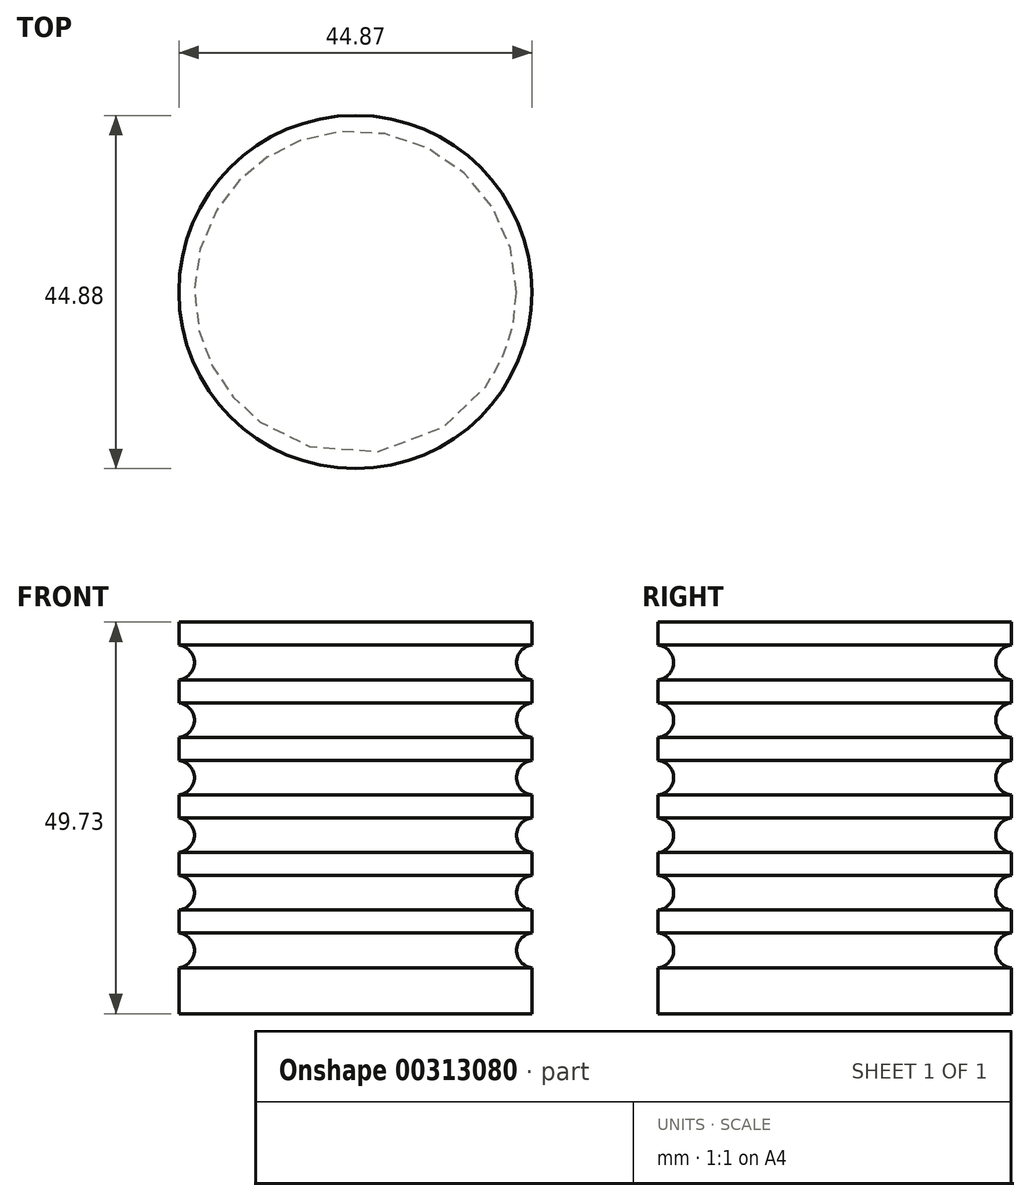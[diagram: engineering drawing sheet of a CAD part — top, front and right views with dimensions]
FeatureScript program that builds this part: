
annotation { "Feature Type Name" : "Feature", "Feature Type Description" : "" }
export const myFeature = defineFeature(function(context is Context, id is Id, definition is map)
    precondition{}
    {
        {
            var Q0;
            Q0=qCreatedBy(makeId("Front.planeOp"),FACE);
            var sketch = newSketch(context, id + "F0", { "sketchPlane" : qUnion([Q0])});
            skLineSegment(sketch, "E0.left", {"start": v(-41.76, 39.6) * mm, "end": v(-41.76, -10.14) * mm});
            skPoint(sketch, "E1.left.start.orphan", {"position": v(-35.66, 9.75) * mm});
            skPoint(sketch, "E0.bottom.end.orphan", {"position": v(-35.66, 39.17) * mm});
            skPoint(sketch, "E0.top.end.orphan", {"position": v(-35.66, -19.66) * mm});
            skLineSegment(sketch, "E2.bottom", {"start": v(-41.76, 39.6) * mm, "end": v(-19.32, 39.6) * mm});
            skLineSegment(sketch, "E2.top", {"start": v(-41.76, -10.14) * mm, "end": v(-19.32, -10.14) * mm});
            skLineSegment(sketch, "E2.right", {"start": v(-19.32, 39.6) * mm, "end": v(-19.32, 36.67) * mm});
            skArc(sketch, "E3", {"start": v(-19.32, 36.67) * mm, "mid": v(-21.3, 34.47) * mm, "end": v(-19.32, 32.28) * mm});
            skArc(sketch, "E4", {"start": v(-19.32, 29.36) * mm, "mid": v(-21.3, 27.16) * mm, "end": v(-19.32, 24.96) * mm});
            skArc(sketch, "E5", {"start": v(-19.32, 22.04) * mm, "mid": v(-21.3, 19.84) * mm, "end": v(-19.32, 17.65) * mm});
            skArc(sketch, "E6", {"start": v(-19.32, 14.73) * mm, "mid": v(-21.3, 12.53) * mm, "end": v(-19.32, 10.33) * mm});
            skArc(sketch, "E7", {"start": v(-19.32, 7.41) * mm, "mid": v(-21.3, 5.21) * mm, "end": v(-19.32, 3.02) * mm});
            skArc(sketch, "E8", {"start": v(-19.32, 0.1) * mm, "mid": v(-21.3, -2.1) * mm, "end": v(-19.32, -4.3) * mm});
            skLineSegment(sketch, "E9.trimOffspring", {"start": v(-19.32, 32.28) * mm, "end": v(-19.32, 29.36) * mm});
            skLineSegment(sketch, "E10.trimOffspring", {"start": v(-19.32, 24.96) * mm, "end": v(-19.32, 22.04) * mm});
            skLineSegment(sketch, "E11.trimOffspring", {"start": v(-19.32, 17.65) * mm, "end": v(-19.32, 14.73) * mm});
            skLineSegment(sketch, "E12.trimOffspring", {"start": v(-19.32, 10.33) * mm, "end": v(-19.32, 7.41) * mm});
            skLineSegment(sketch, "E13.trimOffspring", {"start": v(-19.32, 3.02) * mm, "end": v(-19.32, 0.1) * mm});
            skLineSegment(sketch, "E14.trimOffspring", {"start": v(-19.32, -4.3) * mm, "end": v(-19.32, -10.14) * mm});
            skSolve(sketch);
        }
        {
            var Q0;
            Q0 = qSketchRegion(id + "F0", true);
            var Q1;
            Q1=sQuery(id+"F0.wireOp",EDGE,"E0.left");
            revolve(context, id + "F1", {"entities" : qUnion([Q0]), "axis" : qUnion([Q1]), "revolveType" : RevolveType.FULL});
        }
    });
